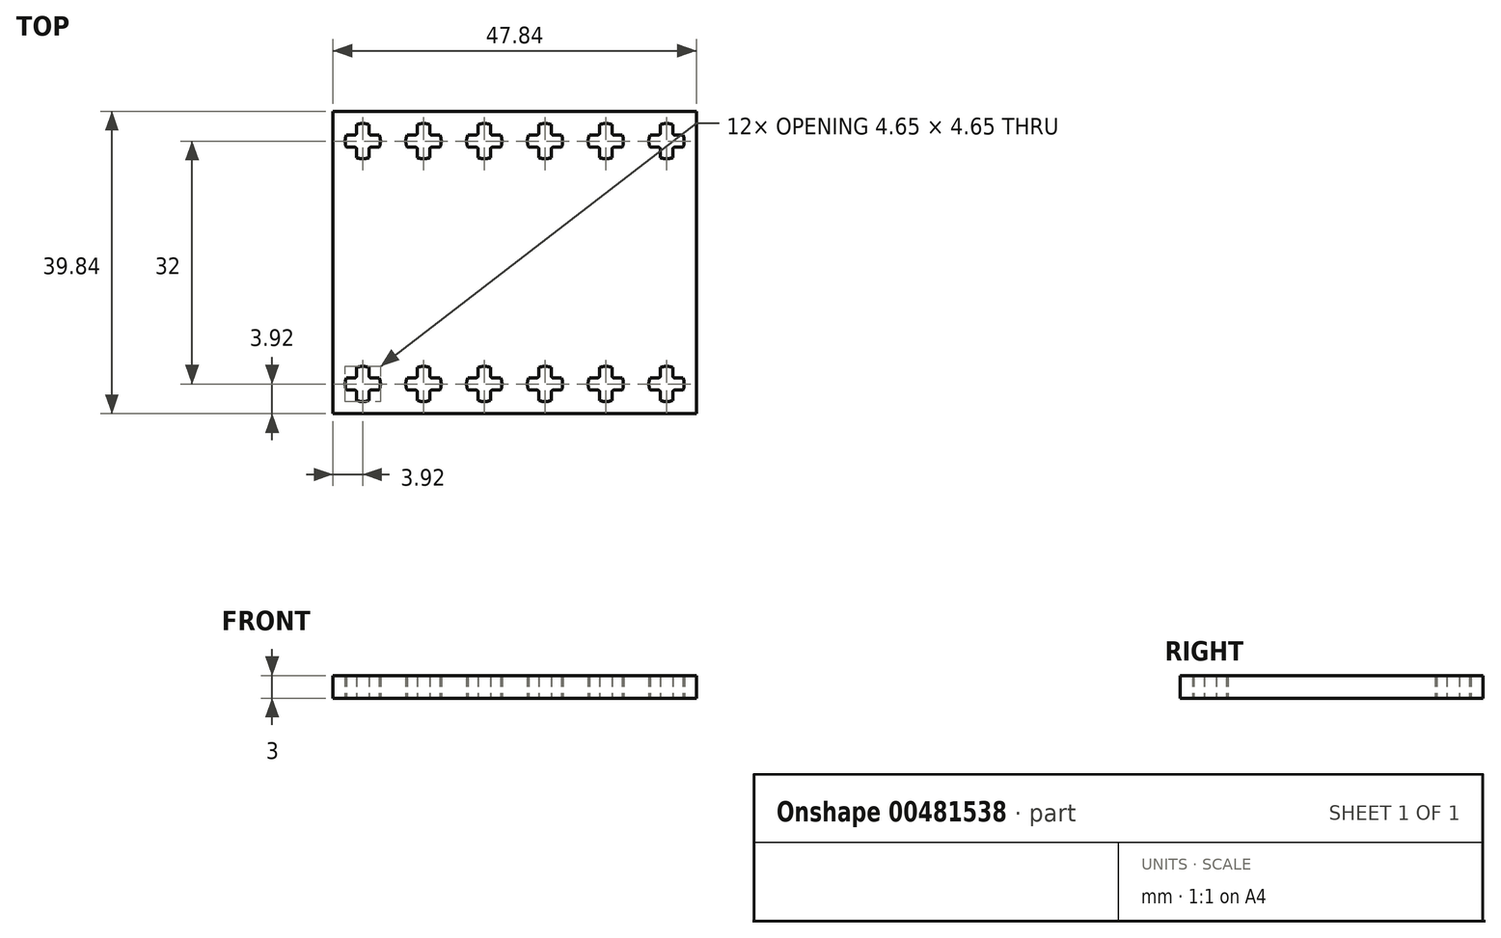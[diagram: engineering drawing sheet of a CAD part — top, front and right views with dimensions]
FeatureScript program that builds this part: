
annotation { "Feature Type Name" : "Feature", "Feature Type Description" : "" }
export const myFeature = defineFeature(function(context is Context, id is Id, definition is map)
    precondition{}
    {
        {
            var Q0;
            Q0=qCreatedBy(makeId("Top.planeOp"),FACE);
            var sketch = newSketch(context, id + "F0", { "sketchPlane" : qUnion([Q0])});
            skLineSegment(sketch, "E0.bottom", {"start": v(-24, 20) * mm, "end": v(24, 20) * mm, "construction": true});
            skLineSegment(sketch, "E0.top", {"start": v(-24, -20) * mm, "end": v(24, -20) * mm, "construction": true});
            skLineSegment(sketch, "E0.left", {"start": v(-24, 20) * mm, "end": v(-24, -20) * mm, "construction": true});
            skLineSegment(sketch, "E0.right", {"start": v(24, 20) * mm, "end": v(24, -20) * mm, "construction": true});
            skLineSegment(sketch, "E1", {"start": v(-20.8, 18.18) * mm, "end": v(-19.2, 18.18) * mm, "construction": true});
            skLineSegment(sketch, "E2", {"start": v(-19.2, 18.18) * mm, "end": v(-19.2, 17.1) * mm});
            skLineSegment(sketch, "E3", {"start": v(-18.9, 16.8) * mm, "end": v(-17.82, 16.8) * mm});
            skLineSegment(sketch, "E4", {"start": v(-17.82, 16.8) * mm, "end": v(-20, 16) * mm, "construction": true});
            skLineSegment(sketch, "E5", {"start": v(-20, 16) * mm, "end": v(-20.8, 18.18) * mm, "construction": true});
            skArc(sketch, "E6", {"start": v(-19.2, 18.18) * mm, "mid": v(-20, 18.32) * mm, "end": v(-20.8, 18.18) * mm});
            skArc(sketch, "E7", {"start": v(-19.2, 17.1) * mm, "mid": v(-19.11, 16.89) * mm, "end": v(-18.9, 16.8) * mm});
            skLineSegment(sketch, "E8", {"start": v(-19.2, 18.18) * mm, "end": v(-19.2, 16.8) * mm, "construction": true});
            skLineSegment(sketch, "E9", {"start": v(-19.2, 16.8) * mm, "end": v(-17.82, 16.8) * mm, "construction": true});
            skArc(sketch, "E10.1.0", {"start": v(-22.18, 16.8) * mm, "mid": v(-22.32, 16) * mm, "end": v(-22.18, 15.2) * mm});
            skArc(sketch, "E10.1.1", {"start": v(-21.1, 16.8) * mm, "mid": v(-20.89, 16.89) * mm, "end": v(-20.8, 17.1) * mm});
            skLineSegment(sketch, "E10.1.2", {"start": v(-22.18, 16.8) * mm, "end": v(-21.1, 16.8) * mm});
            skLineSegment(sketch, "E10.1.3", {"start": v(-20.8, 17.1) * mm, "end": v(-20.8, 18.18) * mm});
            skArc(sketch, "E10.2.0", {"start": v(-20.8, 13.82) * mm, "mid": v(-20, 13.67) * mm, "end": v(-19.2, 13.82) * mm});
            skArc(sketch, "E10.2.1", {"start": v(-20.8, 14.9) * mm, "mid": v(-20.89, 15.11) * mm, "end": v(-21.1, 15.2) * mm});
            skLineSegment(sketch, "E10.2.2", {"start": v(-20.8, 13.82) * mm, "end": v(-20.8, 14.9) * mm});
            skLineSegment(sketch, "E10.2.3", {"start": v(-21.1, 15.2) * mm, "end": v(-22.18, 15.2) * mm});
            skArc(sketch, "E10.3.0", {"start": v(-17.82, 15.2) * mm, "mid": v(-17.67, 16) * mm, "end": v(-17.82, 16.8) * mm});
            skArc(sketch, "E10.3.1", {"start": v(-18.9, 15.2) * mm, "mid": v(-19.11, 15.11) * mm, "end": v(-19.2, 14.9) * mm});
            skLineSegment(sketch, "E10.3.2", {"start": v(-17.82, 15.2) * mm, "end": v(-18.9, 15.2) * mm});
            skLineSegment(sketch, "E10.3.3", {"start": v(-19.2, 14.9) * mm, "end": v(-19.2, 13.82) * mm});
            skArc(sketch, "E11.1.0.0", {"start": v(-11.2, 18.18) * mm, "mid": v(-12, 18.32) * mm, "end": v(-12.8, 18.18) * mm});
            skArc(sketch, "E11.1.0.1", {"start": v(-10.9, 15.2) * mm, "mid": v(-11.11, 15.11) * mm, "end": v(-11.2, 14.9) * mm});
            skLineSegment(sketch, "E11.1.0.2", {"start": v(-9.82, 15.2) * mm, "end": v(-10.9, 15.2) * mm});
            skLineSegment(sketch, "E11.1.0.3", {"start": v(-13.1, 15.2) * mm, "end": v(-14.18, 15.2) * mm});
            skArc(sketch, "E11.1.0.4", {"start": v(-12.8, 14.9) * mm, "mid": v(-12.89, 15.11) * mm, "end": v(-13.1, 15.2) * mm});
            skLineSegment(sketch, "E11.1.0.5", {"start": v(-12.8, 17.1) * mm, "end": v(-12.8, 18.18) * mm});
            skLineSegment(sketch, "E11.1.0.6", {"start": v(-14.18, 16.8) * mm, "end": v(-13.1, 16.8) * mm});
            skArc(sketch, "E11.1.0.7", {"start": v(-13.1, 16.8) * mm, "mid": v(-12.89, 16.89) * mm, "end": v(-12.8, 17.1) * mm});
            skArc(sketch, "E11.1.0.8", {"start": v(-12.8, 13.82) * mm, "mid": v(-12, 13.68) * mm, "end": v(-11.2, 13.82) * mm});
            skArc(sketch, "E11.1.0.9", {"start": v(-14.18, 16.8) * mm, "mid": v(-14.33, 16) * mm, "end": v(-14.18, 15.2) * mm});
            skPoint(sketch, "E11.1.0.10", {"position": v(-12, 16) * mm});
            skLineSegment(sketch, "E11.1.0.11", {"start": v(-12.8, 13.82) * mm, "end": v(-12.8, 14.9) * mm});
            skArc(sketch, "E11.1.0.12", {"start": v(-9.82, 15.2) * mm, "mid": v(-9.68, 16) * mm, "end": v(-9.82, 16.8) * mm});
            skLineSegment(sketch, "E11.1.0.13", {"start": v(-11.2, 14.9) * mm, "end": v(-11.2, 13.82) * mm});
            skLineSegment(sketch, "E11.1.0.14", {"start": v(-11.2, 18.18) * mm, "end": v(-11.2, 17.1) * mm});
            skLineSegment(sketch, "E11.1.0.15", {"start": v(-10.9, 16.8) * mm, "end": v(-9.82, 16.8) * mm});
            skArc(sketch, "E11.1.0.16", {"start": v(-11.2, 17.1) * mm, "mid": v(-11.11, 16.89) * mm, "end": v(-10.9, 16.8) * mm});
            skArc(sketch, "E11.2.0.0", {"start": v(-3.2, 18.18) * mm, "mid": v(-4, 18.32) * mm, "end": v(-4.8, 18.18) * mm});
            skArc(sketch, "E11.2.0.1", {"start": v(-2.9, 15.2) * mm, "mid": v(-3.11, 15.11) * mm, "end": v(-3.2, 14.9) * mm});
            skLineSegment(sketch, "E11.2.0.2", {"start": v(-1.82, 15.2) * mm, "end": v(-2.9, 15.2) * mm});
            skLineSegment(sketch, "E11.2.0.3", {"start": v(-5.1, 15.2) * mm, "end": v(-6.18, 15.2) * mm});
            skArc(sketch, "E11.2.0.4", {"start": v(-4.8, 14.9) * mm, "mid": v(-4.89, 15.11) * mm, "end": v(-5.1, 15.2) * mm});
            skLineSegment(sketch, "E11.2.0.5", {"start": v(-4.8, 17.1) * mm, "end": v(-4.8, 18.18) * mm});
            skLineSegment(sketch, "E11.2.0.6", {"start": v(-6.18, 16.8) * mm, "end": v(-5.1, 16.8) * mm});
            skArc(sketch, "E11.2.0.7", {"start": v(-5.1, 16.8) * mm, "mid": v(-4.89, 16.89) * mm, "end": v(-4.8, 17.1) * mm});
            skArc(sketch, "E11.2.0.8", {"start": v(-4.8, 13.82) * mm, "mid": v(-4, 13.68) * mm, "end": v(-3.2, 13.82) * mm});
            skArc(sketch, "E11.2.0.9", {"start": v(-6.18, 16.8) * mm, "mid": v(-6.33, 16) * mm, "end": v(-6.18, 15.2) * mm});
            skPoint(sketch, "E11.2.0.10", {"position": v(-4, 16) * mm});
            skLineSegment(sketch, "E11.2.0.11", {"start": v(-4.8, 13.82) * mm, "end": v(-4.8, 14.9) * mm});
            skArc(sketch, "E11.2.0.12", {"start": v(-1.82, 15.2) * mm, "mid": v(-1.68, 16) * mm, "end": v(-1.82, 16.8) * mm});
            skLineSegment(sketch, "E11.2.0.13", {"start": v(-3.2, 14.9) * mm, "end": v(-3.2, 13.82) * mm});
            skLineSegment(sketch, "E11.2.0.14", {"start": v(-3.2, 18.18) * mm, "end": v(-3.2, 17.1) * mm});
            skLineSegment(sketch, "E11.2.0.15", {"start": v(-2.9, 16.8) * mm, "end": v(-1.82, 16.8) * mm});
            skArc(sketch, "E11.2.0.16", {"start": v(-3.2, 17.1) * mm, "mid": v(-3.11, 16.89) * mm, "end": v(-2.9, 16.8) * mm});
            skLineSegment(sketch, "E11.direction1", {"start": v(-20.8, 13.82) * mm, "end": v(-12.8, 13.82) * mm, "construction": true});
            skLineSegment(sketch, "E11.direction2", {"start": v(-20.8, 13.82) * mm, "end": v(-20.8, 5.82) * mm, "construction": true});
            skLineSegment(sketch, "E12.bottom", {"start": v(-23.92, 19.92) * mm, "end": v(23.93, 19.92) * mm});
            skLineSegment(sketch, "E12.top", {"start": v(-23.92, -19.93) * mm, "end": v(23.93, -19.93) * mm});
            skLineSegment(sketch, "E12.left", {"start": v(-23.92, 19.92) * mm, "end": v(-23.92, -19.92) * mm});
            skLineSegment(sketch, "E12.right", {"start": v(23.93, 19.92) * mm, "end": v(23.93, -19.92) * mm});
            skArc(sketch, "E13.0.3.0", {"start": v(4.8, 18.18) * mm, "mid": v(4, 18.32) * mm, "end": v(3.2, 18.18) * mm});
            skArc(sketch, "E13.4.3.0", {"start": v(5.1, 15.2) * mm, "mid": v(4.89, 15.11) * mm, "end": v(4.8, 14.9) * mm});
            skLineSegment(sketch, "E13.8.3.0", {"start": v(6.18, 15.2) * mm, "end": v(5.1, 15.2) * mm});
            skLineSegment(sketch, "E13.11.3.0", {"start": v(2.9, 15.2) * mm, "end": v(1.82, 15.2) * mm});
            skArc(sketch, "E13.14.3.0", {"start": v(3.2, 14.9) * mm, "mid": v(3.11, 15.11) * mm, "end": v(2.9, 15.2) * mm});
            skLineSegment(sketch, "E13.18.3.0", {"start": v(3.2, 17.1) * mm, "end": v(3.2, 18.18) * mm});
            skLineSegment(sketch, "E13.21.3.0", {"start": v(1.82, 16.8) * mm, "end": v(2.9, 16.8) * mm});
            skArc(sketch, "E13.24.3.0", {"start": v(2.9, 16.8) * mm, "mid": v(3.11, 16.89) * mm, "end": v(3.2, 17.1) * mm});
            skArc(sketch, "E13.28.3.0", {"start": v(3.2, 13.82) * mm, "mid": v(4, 13.67) * mm, "end": v(4.8, 13.82) * mm});
            skArc(sketch, "E13.32.3.0", {"start": v(1.82, 16.8) * mm, "mid": v(1.67, 16) * mm, "end": v(1.82, 15.2) * mm});
            skPoint(sketch, "E13.36.3.0", {"position": v(4, 16) * mm});
            skLineSegment(sketch, "E13.37.3.0", {"start": v(3.2, 13.82) * mm, "end": v(3.2, 14.9) * mm});
            skArc(sketch, "E13.40.3.0", {"start": v(6.18, 15.2) * mm, "mid": v(6.32, 16) * mm, "end": v(6.18, 16.8) * mm});
            skLineSegment(sketch, "E13.44.3.0", {"start": v(4.8, 14.9) * mm, "end": v(4.8, 13.82) * mm});
            skLineSegment(sketch, "E13.47.3.0", {"start": v(4.8, 18.18) * mm, "end": v(4.8, 17.1) * mm});
            skLineSegment(sketch, "E13.50.3.0", {"start": v(5.1, 16.8) * mm, "end": v(6.18, 16.8) * mm});
            skArc(sketch, "E13.53.3.0", {"start": v(4.8, 17.1) * mm, "mid": v(4.89, 16.89) * mm, "end": v(5.1, 16.8) * mm});
            skArc(sketch, "E14.0.4.0", {"start": v(12.8, 18.18) * mm, "mid": v(12, 18.32) * mm, "end": v(11.2, 18.18) * mm});
            skArc(sketch, "E14.4.4.0", {"start": v(13.1, 15.2) * mm, "mid": v(12.89, 15.11) * mm, "end": v(12.8, 14.9) * mm});
            skLineSegment(sketch, "E14.8.4.0", {"start": v(14.18, 15.2) * mm, "end": v(13.1, 15.2) * mm});
            skLineSegment(sketch, "E14.11.4.0", {"start": v(10.9, 15.2) * mm, "end": v(9.82, 15.2) * mm});
            skArc(sketch, "E14.14.4.0", {"start": v(11.2, 14.9) * mm, "mid": v(11.11, 15.11) * mm, "end": v(10.9, 15.2) * mm});
            skLineSegment(sketch, "E14.18.4.0", {"start": v(11.2, 17.1) * mm, "end": v(11.2, 18.18) * mm});
            skLineSegment(sketch, "E14.21.4.0", {"start": v(9.82, 16.8) * mm, "end": v(10.9, 16.8) * mm});
            skArc(sketch, "E14.24.4.0", {"start": v(10.9, 16.8) * mm, "mid": v(11.11, 16.89) * mm, "end": v(11.2, 17.1) * mm});
            skArc(sketch, "E14.28.4.0", {"start": v(11.2, 13.82) * mm, "mid": v(12, 13.67) * mm, "end": v(12.8, 13.82) * mm});
            skArc(sketch, "E14.32.4.0", {"start": v(9.82, 16.8) * mm, "mid": v(9.67, 16) * mm, "end": v(9.82, 15.2) * mm});
            skPoint(sketch, "E14.36.4.0", {"position": v(12, 16) * mm});
            skLineSegment(sketch, "E14.37.4.0", {"start": v(11.2, 13.82) * mm, "end": v(11.2, 14.9) * mm});
            skArc(sketch, "E14.40.4.0", {"start": v(14.18, 15.2) * mm, "mid": v(14.32, 16) * mm, "end": v(14.18, 16.8) * mm});
            skLineSegment(sketch, "E14.44.4.0", {"start": v(12.8, 14.9) * mm, "end": v(12.8, 13.82) * mm});
            skLineSegment(sketch, "E14.47.4.0", {"start": v(12.8, 18.18) * mm, "end": v(12.8, 17.1) * mm});
            skLineSegment(sketch, "E14.50.4.0", {"start": v(13.1, 16.8) * mm, "end": v(14.18, 16.8) * mm});
            skArc(sketch, "E14.53.4.0", {"start": v(12.8, 17.1) * mm, "mid": v(12.89, 16.89) * mm, "end": v(13.1, 16.8) * mm});
            skLineSegment(sketch, "E15", {"start": v(-24, 16) * mm, "end": v(23.93, 16) * mm, "construction": true});
            skLineSegment(sketch, "E16", {"start": v(-20, 19.92) * mm, "end": v(-20, -20) * mm, "construction": true});
            skLineSegment(sketch, "E17.1.0.0", {"start": v(-24, 8) * mm, "end": v(23.93, 8) * mm, "construction": true});
            skLineSegment(sketch, "E17.2.0.0", {"start": v(-24, 0) * mm, "end": v(23.93, 0) * mm, "construction": true});
            skLineSegment(sketch, "E17.3.0.0", {"start": v(-24, -8) * mm, "end": v(23.93, -8) * mm, "construction": true});
            skLineSegment(sketch, "E17.4.0.0", {"start": v(-24, -16) * mm, "end": v(23.93, -16) * mm, "construction": true});
            skLineSegment(sketch, "E17.5.0.0", {"start": v(-24, -24) * mm, "end": v(23.93, -24) * mm, "construction": true});
            skLineSegment(sketch, "E17.direction1", {"start": v(-24, 16) * mm, "end": v(-24, 8) * mm, "construction": true});
            skLineSegment(sketch, "E18.0.1.0", {"start": v(-12, 19.92) * mm, "end": v(-12, -20) * mm, "construction": true});
            skLineSegment(sketch, "E18.0.2.0", {"start": v(-4, 19.92) * mm, "end": v(-4, -20) * mm, "construction": true});
            skLineSegment(sketch, "E18.0.3.0", {"start": v(4, 19.92) * mm, "end": v(4, -20) * mm, "construction": true});
            skLineSegment(sketch, "E18.0.4.0", {"start": v(12, 19.92) * mm, "end": v(12, -20) * mm, "construction": true});
            skLineSegment(sketch, "E18.direction1", {"start": v(-20, -20) * mm, "end": v(-12, -20) * mm, "construction": true});
            skLineSegment(sketch, "E18.direction2", {"start": v(-20, -20) * mm, "end": v(-12, -20) * mm, "construction": true});
            skArc(sketch, "E19.0.5.0", {"start": v(20.8, 18.18) * mm, "mid": v(20, 18.32) * mm, "end": v(19.2, 18.18) * mm});
            skArc(sketch, "E19.4.5.0", {"start": v(21.1, 15.2) * mm, "mid": v(20.89, 15.11) * mm, "end": v(20.8, 14.9) * mm});
            skLineSegment(sketch, "E19.8.5.0", {"start": v(22.18, 15.2) * mm, "end": v(21.1, 15.2) * mm});
            skLineSegment(sketch, "E19.11.5.0", {"start": v(18.9, 15.2) * mm, "end": v(17.82, 15.2) * mm});
            skArc(sketch, "E19.14.5.0", {"start": v(19.2, 14.9) * mm, "mid": v(19.11, 15.11) * mm, "end": v(18.9, 15.2) * mm});
            skLineSegment(sketch, "E19.18.5.0", {"start": v(19.2, 17.1) * mm, "end": v(19.2, 18.18) * mm});
            skLineSegment(sketch, "E19.21.5.0", {"start": v(17.82, 16.8) * mm, "end": v(18.9, 16.8) * mm});
            skArc(sketch, "E19.24.5.0", {"start": v(18.9, 16.8) * mm, "mid": v(19.11, 16.89) * mm, "end": v(19.2, 17.1) * mm});
            skArc(sketch, "E19.28.5.0", {"start": v(19.2, 13.82) * mm, "mid": v(20, 13.67) * mm, "end": v(20.8, 13.82) * mm});
            skArc(sketch, "E19.32.5.0", {"start": v(17.82, 16.8) * mm, "mid": v(17.68, 16) * mm, "end": v(17.82, 15.2) * mm});
            skPoint(sketch, "E19.36.5.0", {"position": v(20, 16) * mm});
            skLineSegment(sketch, "E19.37.5.0", {"start": v(19.2, 13.82) * mm, "end": v(19.2, 14.9) * mm});
            skArc(sketch, "E19.40.5.0", {"start": v(22.18, 15.2) * mm, "mid": v(22.33, 16) * mm, "end": v(22.18, 16.8) * mm});
            skLineSegment(sketch, "E19.44.5.0", {"start": v(20.8, 14.9) * mm, "end": v(20.8, 13.82) * mm});
            skLineSegment(sketch, "E19.47.5.0", {"start": v(20.8, 18.18) * mm, "end": v(20.8, 17.1) * mm});
            skLineSegment(sketch, "E19.50.5.0", {"start": v(21.1, 16.8) * mm, "end": v(22.18, 16.8) * mm});
            skArc(sketch, "E19.53.5.0", {"start": v(20.8, 17.1) * mm, "mid": v(20.89, 16.89) * mm, "end": v(21.1, 16.8) * mm});
            skLineSegment(sketch, "E20.MirrorCS", {"start": v(-18.9, -16.8) * mm, "end": v(-17.82, -16.8) * mm});
            skLineSegment(sketch, "E21.MirrorCS", {"start": v(-19.2, -18.18) * mm, "end": v(-19.2, -17.1) * mm});
            skLineSegment(sketch, "E22.MirrorCS", {"start": v(-17.82, -16.8) * mm, "end": v(-20, -16) * mm, "construction": true});
            skArc(sketch, "E23.MirrorCS", {"start": v(-19.2, -17.1) * mm, "mid": v(-19.11, -16.89) * mm, "end": v(-18.9, -16.8) * mm});
            skLineSegment(sketch, "E24.MirrorCS", {"start": v(-19.2, -18.18) * mm, "end": v(-19.2, -16.8) * mm, "construction": true});
            skArc(sketch, "E25.MirrorCS", {"start": v(-19.2, -18.18) * mm, "mid": v(-20, -18.32) * mm, "end": v(-20.8, -18.18) * mm});
            skArc(sketch, "E26.MirrorCS", {"start": v(13.1, -15.2) * mm, "mid": v(12.89, -15.11) * mm, "end": v(12.8, -14.9) * mm});
            skLineSegment(sketch, "E27.MirrorCS", {"start": v(-20.8, -18.18) * mm, "end": v(-19.2, -18.18) * mm, "construction": true});
            skArc(sketch, "E28.MirrorCS", {"start": v(5.1, -15.2) * mm, "mid": v(4.89, -15.11) * mm, "end": v(4.8, -14.9) * mm});
            skLineSegment(sketch, "E29.MirrorCS", {"start": v(-19.2, -16.8) * mm, "end": v(-17.82, -16.8) * mm, "construction": true});
            skArc(sketch, "E30.MirrorCS", {"start": v(-18.9, -15.2) * mm, "mid": v(-19.11, -15.11) * mm, "end": v(-19.2, -14.9) * mm});
            skArc(sketch, "E31.MirrorCS", {"start": v(-4.8, -14.9) * mm, "mid": v(-4.89, -15.11) * mm, "end": v(-5.1, -15.2) * mm});
            skArc(sketch, "E32.MirrorCS", {"start": v(4.8, -17.1) * mm, "mid": v(4.89, -16.89) * mm, "end": v(5.1, -16.8) * mm});
            skArc(sketch, "E33.MirrorCS", {"start": v(18.9, -16.8) * mm, "mid": v(19.11, -16.89) * mm, "end": v(19.2, -17.1) * mm});
            skArc(sketch, "E34.MirrorCS", {"start": v(12.8, -17.1) * mm, "mid": v(12.89, -16.89) * mm, "end": v(13.1, -16.8) * mm});
            skArc(sketch, "E35.MirrorCS", {"start": v(-3.2, -17.1) * mm, "mid": v(-3.11, -16.89) * mm, "end": v(-2.9, -16.8) * mm});
            skArc(sketch, "E36.MirrorCS", {"start": v(-20.8, -14.9) * mm, "mid": v(-20.89, -15.11) * mm, "end": v(-21.1, -15.2) * mm});
            skLineSegment(sketch, "E37.MirrorCS", {"start": v(20.8, -14.9) * mm, "end": v(20.8, -13.82) * mm});
            skArc(sketch, "E38.MirrorCS", {"start": v(21.1, -15.2) * mm, "mid": v(20.89, -15.11) * mm, "end": v(20.8, -14.9) * mm});
            skArc(sketch, "E39.MirrorCS", {"start": v(10.9, -16.8) * mm, "mid": v(11.11, -16.89) * mm, "end": v(11.2, -17.1) * mm});
            skArc(sketch, "E40.MirrorCS", {"start": v(-2.9, -15.2) * mm, "mid": v(-3.11, -15.11) * mm, "end": v(-3.2, -14.9) * mm});
            skArc(sketch, "E41.MirrorCS", {"start": v(19.2, -14.9) * mm, "mid": v(19.11, -15.11) * mm, "end": v(18.9, -15.2) * mm});
            skArc(sketch, "E42.MirrorCS", {"start": v(-21.1, -16.8) * mm, "mid": v(-20.89, -16.89) * mm, "end": v(-20.8, -17.1) * mm});
            skArc(sketch, "E43.MirrorCS", {"start": v(20.8, -17.1) * mm, "mid": v(20.89, -16.89) * mm, "end": v(21.1, -16.8) * mm});
            skArc(sketch, "E44.MirrorCS", {"start": v(3.2, -14.9) * mm, "mid": v(3.11, -15.11) * mm, "end": v(2.9, -15.2) * mm});
            skLineSegment(sketch, "E45.MirrorCS", {"start": v(-20.8, -17.1) * mm, "end": v(-20.8, -18.18) * mm});
            skArc(sketch, "E46.MirrorCS", {"start": v(-10.9, -15.2) * mm, "mid": v(-11.11, -15.11) * mm, "end": v(-11.2, -14.9) * mm});
            skArc(sketch, "E47.MirrorCS", {"start": v(2.9, -16.8) * mm, "mid": v(3.11, -16.89) * mm, "end": v(3.2, -17.1) * mm});
            skArc(sketch, "E48.MirrorCS", {"start": v(-5.1, -16.8) * mm, "mid": v(-4.89, -16.89) * mm, "end": v(-4.8, -17.1) * mm});
            skArc(sketch, "E49.MirrorCS", {"start": v(-11.2, -17.1) * mm, "mid": v(-11.11, -16.89) * mm, "end": v(-10.9, -16.8) * mm});
            skLineSegment(sketch, "E50.MirrorCS", {"start": v(-20.8, -13.82) * mm, "end": v(-20.8, -14.9) * mm});
            skLineSegment(sketch, "E51.MirrorCS", {"start": v(-20.8, -13.82) * mm, "end": v(-12.8, -13.82) * mm, "construction": true});
            skLineSegment(sketch, "E52.MirrorCS", {"start": v(-20, -16) * mm, "end": v(-20.8, -18.18) * mm, "construction": true});
            skArc(sketch, "E53.MirrorCS", {"start": v(-9.82, -15.2) * mm, "mid": v(-9.68, -16) * mm, "end": v(-9.82, -16.8) * mm});
            skLineSegment(sketch, "E54.MirrorCS", {"start": v(19.2, -13.82) * mm, "end": v(19.2, -14.9) * mm});
            skLineSegment(sketch, "E55.MirrorCS", {"start": v(-11.2, -14.9) * mm, "end": v(-11.2, -13.82) * mm});
            skLineSegment(sketch, "E56.MirrorCS", {"start": v(21.1, -16.8) * mm, "end": v(22.18, -16.8) * mm});
            skLineSegment(sketch, "E57.MirrorCS", {"start": v(-22.18, -16.8) * mm, "end": v(-21.1, -16.8) * mm});
            skArc(sketch, "E58.MirrorCS", {"start": v(-12.8, -14.9) * mm, "mid": v(-12.89, -15.11) * mm, "end": v(-13.1, -15.2) * mm});
            skLineSegment(sketch, "E59.MirrorCS", {"start": v(13.1, -16.8) * mm, "end": v(14.18, -16.8) * mm});
            skArc(sketch, "E60.MirrorCS", {"start": v(-13.1, -16.8) * mm, "mid": v(-12.89, -16.89) * mm, "end": v(-12.8, -17.1) * mm});
            skLineSegment(sketch, "E61.MirrorCS", {"start": v(-5.1, -15.2) * mm, "end": v(-6.18, -15.2) * mm});
            skLineSegment(sketch, "E62.MirrorCS", {"start": v(19.2, -17.1) * mm, "end": v(19.2, -18.18) * mm});
            skLineSegment(sketch, "E63.MirrorCS", {"start": v(6.18, -15.2) * mm, "end": v(5.1, -15.2) * mm});
            skLineSegment(sketch, "E64.MirrorCS", {"start": v(14.18, -15.2) * mm, "end": v(13.1, -15.2) * mm});
            skLineSegment(sketch, "E65.MirrorCS", {"start": v(17.82, -16.8) * mm, "end": v(18.9, -16.8) * mm});
            skArc(sketch, "E66.MirrorCS", {"start": v(11.2, -13.82) * mm, "mid": v(12, -13.68) * mm, "end": v(12.8, -13.82) * mm});
            skLineSegment(sketch, "E67.MirrorCS", {"start": v(-10.9, -16.8) * mm, "end": v(-9.82, -16.8) * mm});
            skLineSegment(sketch, "E68.MirrorCS", {"start": v(-12.8, -17.1) * mm, "end": v(-12.8, -18.18) * mm});
            skLineSegment(sketch, "E69.MirrorCS", {"start": v(4.8, -14.9) * mm, "end": v(4.8, -13.82) * mm});
            skArc(sketch, "E70.MirrorCS", {"start": v(3.2, -13.82) * mm, "mid": v(4, -13.68) * mm, "end": v(4.8, -13.82) * mm});
            skLineSegment(sketch, "E71.MirrorCS", {"start": v(-17.82, -15.2) * mm, "end": v(-18.9, -15.2) * mm});
            skArc(sketch, "E72.MirrorCS", {"start": v(-11.2, -18.18) * mm, "mid": v(-12, -18.33) * mm, "end": v(-12.8, -18.18) * mm});
            skArc(sketch, "E73.MirrorCS", {"start": v(17.82, -16.8) * mm, "mid": v(17.67, -16) * mm, "end": v(17.82, -15.2) * mm});
            skLineSegment(sketch, "E74.MirrorCS", {"start": v(-12.8, -13.82) * mm, "end": v(-12.8, -14.9) * mm});
            skLineSegment(sketch, "E75.MirrorCS", {"start": v(22.18, -15.2) * mm, "end": v(21.1, -15.2) * mm});
            skLineSegment(sketch, "E76.MirrorCS", {"start": v(11.2, -13.82) * mm, "end": v(11.2, -14.9) * mm});
            skLineSegment(sketch, "E77.MirrorCS", {"start": v(-1.82, -15.2) * mm, "end": v(-2.9, -15.2) * mm});
            skLineSegment(sketch, "E78.MirrorCS", {"start": v(4.8, -18.18) * mm, "end": v(4.8, -17.1) * mm});
            skLineSegment(sketch, "E79.MirrorCS", {"start": v(5.1, -16.8) * mm, "end": v(6.18, -16.8) * mm});
            skArc(sketch, "E80.MirrorCS", {"start": v(-3.2, -18.18) * mm, "mid": v(-4, -18.33) * mm, "end": v(-4.8, -18.18) * mm});
            skLineSegment(sketch, "E81.MirrorCS", {"start": v(-13.1, -15.2) * mm, "end": v(-14.18, -15.2) * mm});
            skLineSegment(sketch, "E82.MirrorCS", {"start": v(-14.18, -16.8) * mm, "end": v(-13.1, -16.8) * mm});
            skArc(sketch, "E83.MirrorCS", {"start": v(20.8, -18.18) * mm, "mid": v(20, -18.33) * mm, "end": v(19.2, -18.18) * mm});
            skArc(sketch, "E84.MirrorCS", {"start": v(19.2, -13.82) * mm, "mid": v(20, -13.68) * mm, "end": v(20.8, -13.82) * mm});
            skLineSegment(sketch, "E85.MirrorCS", {"start": v(-4.8, -17.1) * mm, "end": v(-4.8, -18.18) * mm});
            skLineSegment(sketch, "E86.MirrorCS", {"start": v(-19.2, -14.9) * mm, "end": v(-19.2, -13.82) * mm});
            skLineSegment(sketch, "E87.MirrorCS", {"start": v(-3.2, -18.18) * mm, "end": v(-3.2, -17.1) * mm});
            skArc(sketch, "E88.MirrorCS", {"start": v(4.8, -18.18) * mm, "mid": v(4, -18.33) * mm, "end": v(3.2, -18.18) * mm});
            skArc(sketch, "E89.MirrorCS", {"start": v(-4.8, -13.82) * mm, "mid": v(-4, -13.68) * mm, "end": v(-3.2, -13.82) * mm});
            skArc(sketch, "E90.MirrorCS", {"start": v(-14.18, -16.8) * mm, "mid": v(-14.33, -16) * mm, "end": v(-14.18, -15.2) * mm});
            skLineSegment(sketch, "E91.MirrorCS", {"start": v(-3.2, -14.9) * mm, "end": v(-3.2, -13.82) * mm});
            skArc(sketch, "E92.MirrorCS", {"start": v(-22.18, -16.8) * mm, "mid": v(-22.32, -16) * mm, "end": v(-22.18, -15.2) * mm});
            skLineSegment(sketch, "E93.MirrorCS", {"start": v(-21.1, -15.2) * mm, "end": v(-22.18, -15.2) * mm});
            skLineSegment(sketch, "E94.MirrorCS", {"start": v(9.82, -16.8) * mm, "end": v(10.9, -16.8) * mm});
            skArc(sketch, "E95.MirrorCS", {"start": v(12.8, -18.18) * mm, "mid": v(12, -18.33) * mm, "end": v(11.2, -18.18) * mm});
            skArc(sketch, "E96.MirrorCS", {"start": v(14.18, -15.2) * mm, "mid": v(14.32, -16) * mm, "end": v(14.18, -16.8) * mm});
            skArc(sketch, "E97.MirrorCS", {"start": v(-17.82, -15.2) * mm, "mid": v(-17.68, -16) * mm, "end": v(-17.82, -16.8) * mm});
            skArc(sketch, "E98.MirrorCS", {"start": v(-12.8, -13.82) * mm, "mid": v(-12, -13.68) * mm, "end": v(-11.2, -13.82) * mm});
            skLineSegment(sketch, "E99.MirrorCS", {"start": v(12.8, -14.9) * mm, "end": v(12.8, -13.82) * mm});
            skLineSegment(sketch, "E100.MirrorCS", {"start": v(3.2, -17.1) * mm, "end": v(3.2, -18.18) * mm});
            skLineSegment(sketch, "E101.MirrorCS", {"start": v(20.8, -18.18) * mm, "end": v(20.8, -17.1) * mm});
            skLineSegment(sketch, "E102.MirrorCS", {"start": v(2.9, -15.2) * mm, "end": v(1.82, -15.2) * mm});
            skArc(sketch, "E103.MirrorCS", {"start": v(-1.82, -15.2) * mm, "mid": v(-1.68, -16) * mm, "end": v(-1.82, -16.8) * mm});
            skLineSegment(sketch, "E104.MirrorCS", {"start": v(10.9, -15.2) * mm, "end": v(9.82, -15.2) * mm});
            skLineSegment(sketch, "E105.MirrorCS", {"start": v(1.82, -16.8) * mm, "end": v(2.9, -16.8) * mm});
            skLineSegment(sketch, "E106.MirrorCS", {"start": v(-2.9, -16.8) * mm, "end": v(-1.82, -16.8) * mm});
            skArc(sketch, "E107.MirrorCS", {"start": v(22.18, -15.2) * mm, "mid": v(22.32, -16) * mm, "end": v(22.18, -16.8) * mm});
            skLineSegment(sketch, "E108.MirrorCS", {"start": v(3.2, -13.82) * mm, "end": v(3.2, -14.9) * mm});
            skLineSegment(sketch, "E109.MirrorCS", {"start": v(12.8, -18.18) * mm, "end": v(12.8, -17.1) * mm});
            skLineSegment(sketch, "E110.MirrorCS", {"start": v(18.9, -15.2) * mm, "end": v(17.82, -15.2) * mm});
            skArc(sketch, "E111.MirrorCS", {"start": v(9.82, -16.8) * mm, "mid": v(9.67, -16) * mm, "end": v(9.82, -15.2) * mm});
            skArc(sketch, "E112.MirrorCS", {"start": v(1.82, -16.8) * mm, "mid": v(1.67, -16) * mm, "end": v(1.82, -15.2) * mm});
            skLineSegment(sketch, "E113.MirrorCS", {"start": v(11.2, -17.1) * mm, "end": v(11.2, -18.18) * mm});
            skLineSegment(sketch, "E114.MirrorCS", {"start": v(-9.82, -15.2) * mm, "end": v(-10.9, -15.2) * mm});
            skArc(sketch, "E115.MirrorCS", {"start": v(-20.8, -13.82) * mm, "mid": v(-20, -13.68) * mm, "end": v(-19.2, -13.82) * mm});
            skArc(sketch, "E116.MirrorCS", {"start": v(-6.18, -16.8) * mm, "mid": v(-6.33, -16) * mm, "end": v(-6.18, -15.2) * mm});
            skLineSegment(sketch, "E117.MirrorCS", {"start": v(-4.8, -13.82) * mm, "end": v(-4.8, -14.9) * mm});
            skArc(sketch, "E118.MirrorCS", {"start": v(6.18, -15.2) * mm, "mid": v(6.32, -16) * mm, "end": v(6.18, -16.8) * mm});
            skLineSegment(sketch, "E119.MirrorCS", {"start": v(-11.2, -18.18) * mm, "end": v(-11.2, -17.1) * mm});
            skLineSegment(sketch, "E120.MirrorCS", {"start": v(-6.18, -16.8) * mm, "end": v(-5.1, -16.8) * mm});
            skArc(sketch, "E121.MirrorCS", {"start": v(11.2, -14.9) * mm, "mid": v(11.11, -15.11) * mm, "end": v(10.9, -15.2) * mm});
            skSolve(sketch);
        }
        {
            var Q0;
            Q0=makeQuery(id+"F0.imprint","IMPRINT",FACE,{"disambiguationData":[TD([[makeQuery(id+"F0.imprint","IMPRINT",EDGE,{"derivedFrom":sQuery(id+"F0.wireOp",EDGE,"E2")}),1.0]])]});
            extrude(context, id + "F1", {"entities" : qUnion([Q0]), "depth" : 3 * mm, "offsetDistance" : 25 * mm});
        }
    });
